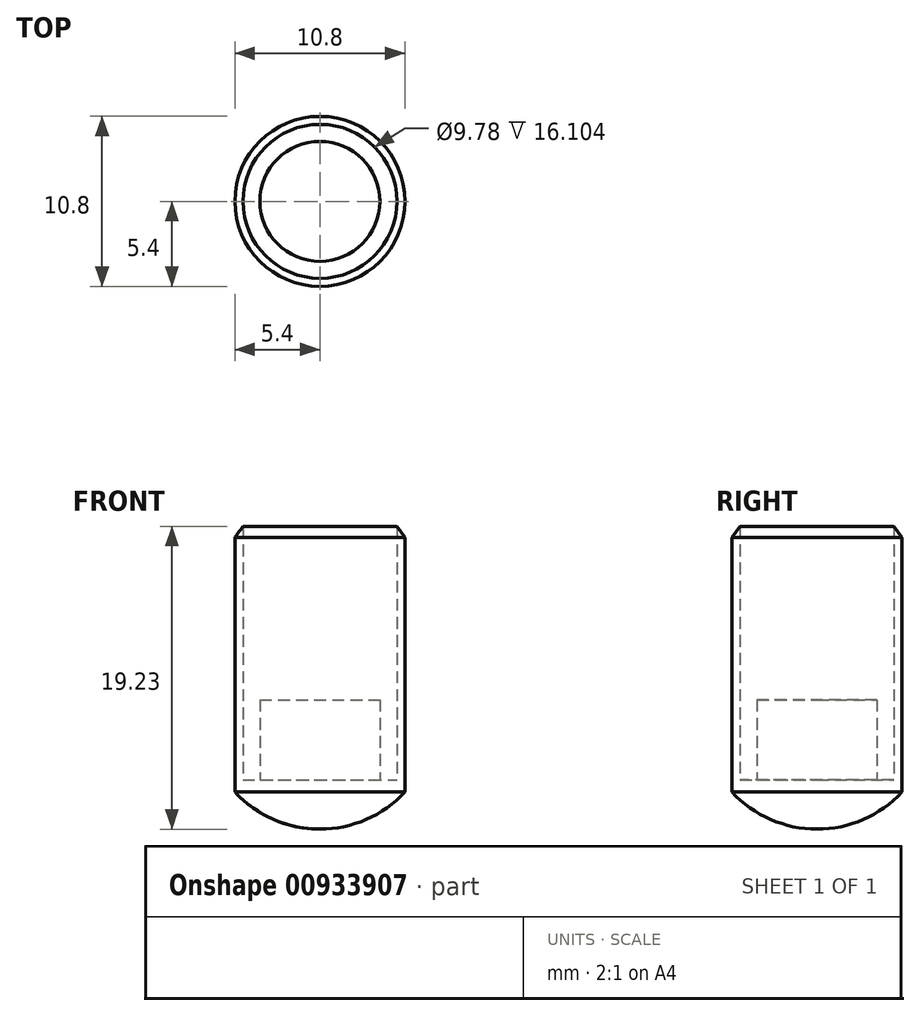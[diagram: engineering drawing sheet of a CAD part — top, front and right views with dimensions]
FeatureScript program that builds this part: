
annotation { "Feature Type Name" : "Feature", "Feature Type Description" : "" }
export const myFeature = defineFeature(function(context is Context, id is Id, definition is map)
    precondition{}
    {
        {
            var Q0;
            Q0=qCreatedBy(makeId("Front.planeOp"),FACE);
            var sketch = newSketch(context, id + "F0", { "sketchPlane" : qUnion([Q0])});
            skArc(sketch, "E0", {"start": v(-7.37, 0) * mm, "mid": v(-5.2, -5.2) * mm, "end": v(0, -7.37) * mm});
            skLineSegment(sketch, "E1", {"start": v(0, -7.37) * mm, "end": v(0, -4.23) * mm});
            skLineSegment(sketch, "E2.bottom", {"start": v(-3.81, -4.24) * mm, "end": v(-4.89, -4.24) * mm});
            skLineSegment(sketch, "E2.right", {"start": v(-4.89, -4.24) * mm, "end": v(-4.89, 4.24) * mm});
            skLineSegment(sketch, "E3", {"start": v(-7.37, 0) * mm, "end": v(-7.37, 8.46) * mm});
            skLineSegment(sketch, "E4", {"start": v(-4.89, 4.24) * mm, "end": v(-4.89, 11.86) * mm});
            skLineSegment(sketch, "E5", {"start": v(-7.37, 8.46) * mm, "end": v(-4.89, 11.86) * mm});
            skPoint(sketch, "E2.left.end.orphan", {"position": v(4.89, 4.24) * mm});
            skPoint(sketch, "E6.orphan", {"position": v(4.89, -4.24) * mm});
            skPoint(sketch, "E7.orphan", {"position": v(7.37, 0) * mm});
            skLineSegment(sketch, "E8", {"start": v(0, -4.23) * mm, "end": v(0, 0.85) * mm});
            skLineSegment(sketch, "E9", {"start": v(0, 0.85) * mm, "end": v(-3.81, 0.85) * mm});
            skLineSegment(sketch, "E10", {"start": v(-3.81, 0.85) * mm, "end": v(-3.81, -4.24) * mm});
            skSolve(sketch);
        }
        {
            var Q0;
            Q0=makeQuery(id+"F0.imprint","IMPRINT",FACE,{"disambiguationData":[TD([[makeQuery(id+"F0.imprint","IMPRINT",EDGE,{"derivedFrom":sQuery(id+"F0.wireOp",EDGE,"E0")}),1.0]])]});
            var Q1;
            Q1=sQuery(id+"F0.wireOp",EDGE,"E8");
            revolve(context, id + "F1", {"surfaceOperationType" : NewSurfaceOperationType.NEW, "entities" : qUnion([Q0]), "axis" : qUnion([Q1]), "revolveType" : RevolveType.FULL});
        }
        {
            var Q0;
            Q0=qCreatedBy(makeId("Top.planeOp"),FACE);
            cPlane(context, id + "F2", {"entities" : qUnion([Q0]), "cplaneType" : CPlaneType.OFFSET, "offset" : 12.7 * mm, "width" : 152.4 * mm, "height" : 152.4 * mm});
        }
        {
            var Q0;
            Q0=qCreatedBy(id+"F2.planeOp",FACE);
            var sketch = newSketch(context, id + "F3", { "sketchPlane" : qUnion([Q0])});
            skCircle(sketch, "E11", {"center": v(0, 0) * mm, "radius": 5.4 * mm});
            skCircle(sketch, "E12", {"center": v(0, 0) * mm, "radius": 7.37 * mm});
            skSolve(sketch);
        }
        {
            var Q0;
            Q0=makeQuery(id+"F3.imprint","IMPRINT",FACE,{"disambiguationData":[TD([[makeQuery(id+"F3.imprint","IMPRINT",EDGE,{"derivedFrom":sQuery(id+"F3.wireOp",EDGE,"E11")}),-1.0]])]});
            extrude(context, id + "F4", {"entities" : qUnion([Q0]), "operationType" : NewBodyOperationType.REMOVE, "oppositeDirection" : true, "depth" : 25.4 * mm, "offsetDistance" : 25.4 * mm});
        }
    });
